# Revit family: Domotics-DomesticRanges-GEWISS-SYSTEM_POWER-SOCKET-OUTLET_USA
name_source: partatom
category: Apparecchi elettrici
revit_build: Autodesk Revit 2016 (Build: 20161004_0715(x64)
units: mm (PartAtom-declared; Revit-internal decimal feet)

## family parameters
Condiviso = Sì
Host = Superficie
Mantenere orientamento annotazione = Sì
Punto di calcolo locali = Sì
Quota connettore circolare = Usa diametro
Taglio con vuoti quando caricato = Sì
Tipo di parte = Normale

## types (2) — shared parameters
Carico apparente = 0 VA
Catalogue = DOMOTICS
Catalogue Range = SYSTEM - DOMESTIC RANGE
Description. = USA
Electrocod = 0131
For plug pins = Flat
IDF = c0ed77c7-f079-4b1f-9b87-2b0a27c530df
IDT = ee7472e3-5b00-4676-9de9-5bd574cc3f56
Immagine tipo = GW21216.jpg
N. poli = 1
No. SYSTEM modules = 1
Produttore = GEWISS S.p.A.
Prospetto di default = 1219 mm
SEO = Socket outlet
Shape = Aligned vertical
Standard = USA
Standard: = USA
TXT ELETTRICO = 15
Technical sheet = https://www.gewiss.com
Tipo_ = System Prese Usa_GENERICO : GW21216 Presa 2P+T 15A 250V standard USA nero
URL = https://www.gewiss.com
Version file RFA = 19.4
Volt = 230 V
Voltage = 250/125V AC
Voltage: = 250/125V AC

## per-type parameters (varying)
| type | Colour | Description: | Descrizione | EAN code | Modello |
| GW21216 - 2P+E 15A 250V usa s.-outlet black | Black | 2P+E - 15A 250V ac | 2P+E 15A 250V USA S.-OUTLET SY/BK | 8011564128552 | GW21216 |
| GW20216 - 2P+E 15A 250V usa s.-outlet white | White | 2P+E - 15A - 250V ac | 2P+E 15A 250V USA S.-OUTLET SY/WT | 8011564000698 | GW20216 |

## geometry (parser evidence)
native form markers: Sweep x1
no freeform markers — native parametric forms only
